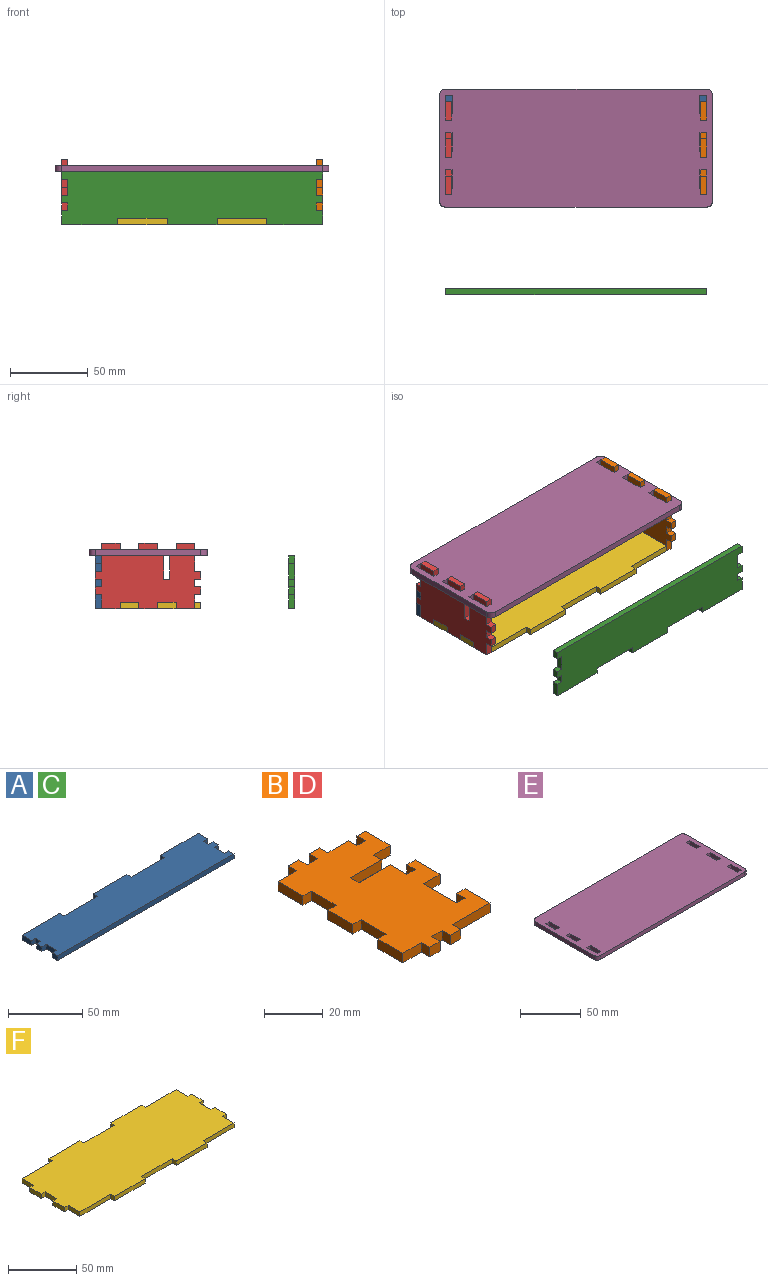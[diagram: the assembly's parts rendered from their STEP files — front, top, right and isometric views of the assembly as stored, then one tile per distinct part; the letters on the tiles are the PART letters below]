
ASSEMBLY  parts=6 mates=5
PART A: 30 faces, bbox 168x34x4 mm
  f0: plane 5x4mm, normal (1,0,0), area 20mm2, adj f1,f27,f28,f29
  f1: plane 4x4mm, normal (0,-1,0), area 16mm2, adj f0,f2,f28,f29
  f2: plane 9x4mm, normal (1,0,0), area 36mm2, adj f1,f3,f28,f29
  f3: plane 36x4mm, normal (0,1,0), area 144mm2, adj f2,f4,f28,f29
  f4: plane 4x4mm, normal (-1,0,0), area 16mm2, adj f3,f5,f28,f29
  f5: plane 32x4mm, normal (0,1,0), area 128mm2, adj f4,f6,f28,f29
  f6: plane 4x4mm, normal (1,0,0), area 16mm2, adj f5,f7,f28,f29
  f7: plane 32x4mm, normal (0,1,0), area 128mm2, adj f6,f8,f28,f29
  f8: plane 4x4mm, normal (-1,0,0), area 16mm2, adj f7,f9,f28,f29
  f9: plane 32x4mm, normal (0,1,0), area 128mm2, adj f8,f10,f28,f29
  f10: plane 4x4mm, normal (1,0,0), area 16mm2, adj f9,f11,f28,f29
  f11: plane 36x4mm, normal (0,1,0), area 144mm2, adj f10,f12,f28,f29
  f12: plane 9x4mm, normal (-1,0,0), area 36mm2, adj f11,f13,f28,f29
  f13: plane 4x4mm, normal (0,-1,0), area 16mm2, adj f12,f14,f28,f29
  f14: plane 5x4mm, normal (-1,0,0), area 20mm2, adj f13,f15,f28,f29
  f15: plane 4x4mm, normal (0,1,0), area 16mm2, adj f14,f16,f28,f29
  f16: plane 5x4mm, normal (-1,0,0), area 20mm2, adj f15,f17,f28,f29
  f17: plane 4x4mm, normal (0,-1,0), area 16mm2, adj f16,f18,f28,f29
  f18: plane 10x4mm, normal (-1,0,0), area 40mm2, adj f17,f19,f28,f29
  f19: plane 4x4mm, normal (0,1,0), area 16mm2, adj f18,f20,f28,f29
  f20: plane 5x4mm, normal (-1,0,0), area 20mm2, adj f19,f21,f28,f29
  f21: plane 168x4mm, normal (0,-1,0), area 672mm2, adj f20,f22,f28,f29
  f22: plane 5x4mm, normal (1,0,0), area 20mm2, adj f21,f23,f28,f29
  f23: plane 4x4mm, normal (0,1,0), area 16mm2, adj f22,f24,f28,f29
  f24: plane 10x4mm, normal (1,0,0), area 40mm2, adj f23,f25,f28,f29
  f25: plane 4x4mm, normal (0,-1,0), area 16mm2, adj f24,f26,f28,f29
  f26: plane 5x4mm, normal (1,0,0), area 20mm2, adj f25,f27,f28,f29
  f27: plane 4x4mm, normal (0,1,0), area 16mm2, adj f0,f26,f28,f29
  f28: plane 168x34mm, normal (0,0,1), area 5336mm2, adj f0,f1,f2,f3,f4,f5,f6,f7
  f29: plane 168x34mm, normal (0,0,-1), area 5336mm2, adj f0,f1,f2,f3,f4,f5,f6,f7
PART B: 50 faces, bbox 42x68x4 mm
  f0: plane 4x4mm, normal (1,0,0), area 16mm2, adj f1,f47,f48,f49
  f1: plane 8x4mm, normal (0,-1,0), area 32mm2, adj f0,f2,f48,f49
  f2: plane 12x4mm, normal (1,0,0), area 48mm2, adj f1,f3,f48,f49
  f3: plane 4x4mm, normal (0,1,0), area 16mm2, adj f2,f4,f48,f49
  f4: plane 4x4mm, normal (-1,0,0), area 16mm2, adj f3,f5,f48,f49
  f5: plane 4x4mm, normal (0,1,0), area 16mm2, adj f4,f6,f48,f49
  f6: plane 4x4mm, normal (1,0,0), area 16mm2, adj f5,f7,f48,f49
  f7: plane 10x4mm, normal (0,1,0), area 40mm2, adj f6,f8,f48,f49
  f8: plane 4x4mm, normal (1,0,0), area 16mm2, adj f7,f9,f48,f49
  f9: plane 5x4mm, normal (0,1,0), area 20mm2, adj f8,f10,f48,f49
  f10: plane 4x4mm, normal (-1,0,0), area 16mm2, adj f9,f11,f48,f49
  f11: plane 5x4mm, normal (0,1,0), area 20mm2, adj f10,f12,f48,f49
  f12: plane 4x4mm, normal (1,0,0), area 16mm2, adj f11,f13,f48,f49
  f13: plane 5x4mm, normal (0,1,0), area 20mm2, adj f12,f14,f48,f49
  f14: plane 4x4mm, normal (-1,0,0), area 16mm2, adj f13,f15,f48,f49
  f15: plane 9x4mm, normal (0,1,0), area 36mm2, adj f14,f16,f48,f49
  f16: plane 12x4mm, normal (-1,0,0), area 48mm2, adj f15,f17,f48,f49
  f17: plane 4x4mm, normal (0,-1,0), area 16mm2, adj f16,f18,f48,f49
  f18: plane 12x4mm, normal (-1,0,0), area 48mm2, adj f17,f19,f48,f49
  f19: plane 4x4mm, normal (0,1,0), area 16mm2, adj f18,f20,f48,f49
  f20: plane 12x4mm, normal (-1,0,0), area 48mm2, adj f19,f21,f48,f49
  f21: plane 4x4mm, normal (0,-1,0), area 16mm2, adj f20,f22,f48,f49
  f22: plane 12x4mm, normal (-1,0,0), area 48mm2, adj f21,f23,f48,f49
  f23: plane 4x4mm, normal (0,1,0), area 16mm2, adj f22,f24,f48,f49
  f24: plane 12x4mm, normal (-1,0,0), area 48mm2, adj f23,f25,f48,f49
  f25: plane 9x4mm, normal (0,-1,0), area 36mm2, adj f24,f26,f48,f49
  f26: plane 4x4mm, normal (-1,0,0), area 16mm2, adj f25,f27,f48,f49
  f27: plane 5x4mm, normal (0,-1,0), area 20mm2, adj f26,f28,f48,f49
  f28: plane 4x4mm, normal (1,0,0), area 16mm2, adj f27,f29,f48,f49
  f29: plane 5x4mm, normal (0,-1,0), area 20mm2, adj f28,f30,f48,f49
  f30: plane 4x4mm, normal (-1,0,0), area 16mm2, adj f29,f31,f48,f49
  f31: plane 5x4mm, normal (0,-1,0), area 20mm2, adj f30,f32,f48,f49
  f32: plane 4x4mm, normal (1,0,0), area 16mm2, adj f31,f33,f48,f49
  f33: plane 18x4mm, normal (0,-1,0), area 72mm2, adj f32,f34,f48,f49
  f34: plane 12x4mm, normal (1,0,0), area 48mm2, adj f33,f35,f48,f49
  f35: plane 4x4mm, normal (0,1,0), area 16mm2, adj f34,f36,f48,f49
  f36: plane 4x4mm, normal (-1,0,0), area 16mm2, adj f35,f37,f48,f49
  f37: plane 4x4mm, normal (0,1,0), area 16mm2, adj f36,f38,f48,f49
  f38: plane 16x4mm, normal (1,0,0), area 64mm2, adj f37,f39,f48,f49
  f39: plane 8x4mm, normal (0,-1,0), area 32mm2, adj f38,f40,f48,f49
  f40: plane 12x4mm, normal (1,0,0), area 48mm2, adj f39,f41,f48,f49
  f41: plane 4x4mm, normal (0,1,0), area 16mm2, adj f40,f42,f48,f49
  f42: plane 4x4mm, normal (-1,0,0), area 16mm2, adj f41,f43,f48,f49
  f43: plane 4x4mm, normal (0,1,0), area 16mm2, adj f42,f44,f48,f49
  f44: plane 8x4mm, normal (1,0,0), area 32mm2, adj f43,f45,f48,f49
  f45: plane 15x4mm, normal (0,1,0), area 60mm2, adj f44,f46,f48,f49
  f46: plane 4x4mm, normal (1,0,0), area 16mm2, adj f45,f47,f48,f49
  f47: plane 15x4mm, normal (0,-1,0), area 60mm2, adj f0,f46,f48,f49
  f48: plane 68x42mm, normal (0,0,1), area 2204mm2, adj f0,f1,f2,f3,f4,f5,f6,f7
  f49: plane 68x42mm, normal (0,0,-1), area 2204mm2, adj f0,f1,f2,f3,f4,f5,f6,f7
PART C: same geometry as A
PART D: same geometry as B
PART E: 34 faces, bbox 176x76x4 mm
  f0: plane 12x4mm, normal (-1,0,0), area 48mm2, adj f1,f27,f28,f29
  f1: plane 4.2x4mm, normal (0,1,0), area 16.8mm2, adj f0,f2,f28,f29
  f2: plane 12x4mm, normal (1,0,0), area 48mm2, adj f1,f27,f28,f29
  f3: plane 12x4mm, normal (-1,0,0), area 48mm2, adj f4,f21,f28,f29
  f4: plane 4.2x4mm, normal (0,1,0), area 16.8mm2, adj f3,f5,f28,f29
  f5: plane 12x4mm, normal (1,0,0), area 48mm2, adj f4,f21,f28,f29
  f6: plane 12x4mm, normal (1,0,0), area 48mm2, adj f7,f22,f28,f29
  f7: plane 4.2x4mm, normal (0,-1,0), area 16.8mm2, adj f6,f8,f28,f29
  f8: plane 12x4mm, normal (-1,0,0), area 48mm2, adj f7,f22,f28,f29
  f9: plane 68x4mm, normal (-1,0,0), area 272mm2, adj f28,f29,f30,f33
  f10: plane 168x4mm, normal (0,-1,0), area 672mm2, adj f28,f29,f30,f31
  f11: plane 68x4mm, normal (1,0,0), area 272mm2, adj f28,f29,f31,f32
  f12: plane 12x4mm, normal (-1,0,0), area 48mm2, adj f13,f24,f28,f29
  f13: plane 4.2x4mm, normal (0,1,0), area 16.8mm2, adj f12,f14,f28,f29
  f14: plane 12x4mm, normal (1,0,0), area 48mm2, adj f13,f24,f28,f29
  f15: plane 12x4mm, normal (-1,0,0), area 48mm2, adj f16,f25,f28,f29
  f16: plane 4.2x4mm, normal (0,1,0), area 16.8mm2, adj f15,f17,f28,f29
  f17: plane 12x4mm, normal (1,0,0), area 48mm2, adj f16,f25,f28,f29
  f18: plane 12x4mm, normal (-1,0,0), area 48mm2, adj f19,f26,f28,f29
  f19: plane 4.2x4mm, normal (0,1,0), area 16.8mm2, adj f18,f20,f28,f29
  f20: plane 12x4mm, normal (1,0,0), area 48mm2, adj f19,f26,f28,f29
  f21: plane 4.2x4mm, normal (0,-1,0), area 16.8mm2, adj f3,f5,f28,f29
  f22: plane 4.2x4mm, normal (0,1,0), area 16.8mm2, adj f6,f8,f28,f29
  f23: plane 168x4mm, normal (0,1,0), area 672mm2, adj f28,f29,f32,f33
  f24: plane 4.2x4mm, normal (0,-1,0), area 16.8mm2, adj f12,f14,f28,f29
  f25: plane 4.2x4mm, normal (0,-1,0), area 16.8mm2, adj f15,f17,f28,f29
  f26: plane 4.2x4mm, normal (0,-1,0), area 16.8mm2, adj f18,f20,f28,f29
  f27: plane 4.2x4mm, normal (0,-1,0), area 16.8mm2, adj f0,f2,f28,f29
  f28: plane 176x76mm, normal (0,0,1), area 13059.9mm2, adj f0,f1,f2,f3,f4,f5,f6,f7
  f29: plane 176x76mm, normal (0,0,-1), area 13059.9mm2, adj f0,f1,f2,f3,f4,f5,f6,f7
  f30: cylinder r=4mm len=4mm, axis (0,0,-1), area 25.1mm2, adj f9,f10,f28,f29
  f31: cylinder r=4mm len=4mm, axis (0,0,-1), area 25.1mm2, adj f10,f11,f28,f29
  f32: cylinder r=4mm len=4mm, axis (0,0,-1), area 25.1mm2, adj f11,f23,f28,f29
  f33: cylinder r=4mm len=4mm, axis (0,0,-1), area 25.1mm2, adj f9,f23,f28,f29
PART F: 38 faces, bbox 168x68x4 mm
  f0: plane 4x4mm, normal (-1,0,0), area 16mm2, adj f1,f35,f36,f37
  f1: plane 32x4mm, normal (0,-1,0), area 128mm2, adj f0,f2,f36,f37
  f2: plane 4x4mm, normal (1,0,0), area 16mm2, adj f1,f3,f36,f37
  f3: plane 32x4mm, normal (0,-1,0), area 128mm2, adj f2,f4,f36,f37
  f4: plane 4x4mm, normal (-1,0,0), area 16mm2, adj f3,f5,f36,f37
  f5: plane 32x4mm, normal (0,-1,0), area 128mm2, adj f4,f6,f36,f37
  f6: plane 4x4mm, normal (1,0,0), area 16mm2, adj f5,f7,f36,f37
  f7: plane 32x4mm, normal (0,-1,0), area 128mm2, adj f6,f8,f36,f37
  f8: plane 12x4mm, normal (1,0,0), area 48mm2, adj f7,f9,f36,f37
  f9: plane 4x4mm, normal (0,-1,0), area 16mm2, adj f8,f10,f36,f37
  f10: plane 12x4mm, normal (1,0,0), area 48mm2, adj f9,f11,f36,f37
  f11: plane 4x4mm, normal (0,1,0), area 16mm2, adj f10,f12,f36,f37
  f12: plane 12x4mm, normal (1,0,0), area 48mm2, adj f11,f13,f36,f37
  f13: plane 4x4mm, normal (0,-1,0), area 16mm2, adj f12,f14,f36,f37
  f14: plane 12x4mm, normal (1,0,0), area 48mm2, adj f13,f15,f36,f37
  f15: plane 4x4mm, normal (0,1,0), area 16mm2, adj f14,f16,f36,f37
  f16: plane 12x4mm, normal (1,0,0), area 48mm2, adj f15,f17,f36,f37
  f17: plane 32x4mm, normal (0,1,0), area 128mm2, adj f16,f18,f36,f37
  f18: plane 4x4mm, normal (1,0,0), area 16mm2, adj f17,f19,f36,f37
  f19: plane 32x4mm, normal (0,1,0), area 128mm2, adj f18,f20,f36,f37
  f20: plane 4x4mm, normal (-1,0,0), area 16mm2, adj f19,f21,f36,f37
  f21: plane 32x4mm, normal (0,1,0), area 128mm2, adj f20,f22,f36,f37
  f22: plane 4x4mm, normal (1,0,0), area 16mm2, adj f21,f23,f36,f37
  f23: plane 32x4mm, normal (0,1,0), area 128mm2, adj f22,f24,f36,f37
  f24: plane 4x4mm, normal (-1,0,0), area 16mm2, adj f23,f25,f36,f37
  f25: plane 32x4mm, normal (0,1,0), area 128mm2, adj f24,f26,f36,f37
  f26: plane 12x4mm, normal (-1,0,0), area 48mm2, adj f25,f27,f36,f37
  f27: plane 4x4mm, normal (0,1,0), area 16mm2, adj f26,f28,f36,f37
  f28: plane 12x4mm, normal (-1,0,0), area 48mm2, adj f27,f29,f36,f37
  f29: plane 4x4mm, normal (0,-1,0), area 16mm2, adj f28,f30,f36,f37
  f30: plane 12x4mm, normal (-1,0,0), area 48mm2, adj f29,f31,f36,f37
  f31: plane 4x4mm, normal (0,1,0), area 16mm2, adj f30,f32,f36,f37
  f32: plane 12x4mm, normal (-1,0,0), area 48mm2, adj f31,f33,f36,f37
  f33: plane 4x4mm, normal (0,-1,0), area 16mm2, adj f32,f34,f36,f37
  f34: plane 12x4mm, normal (-1,0,0), area 48mm2, adj f33,f35,f36,f37
  f35: plane 32x4mm, normal (0,-1,0), area 128mm2, adj f0,f34,f36,f37
  f36: plane 168x68mm, normal (0,0,1), area 10304mm2, adj f0,f1,f2,f3,f4,f5,f6,f7
  f37: plane 168x68mm, normal (0,0,-1), area 10304mm2, adj f0,f1,f2,f3,f4,f5,f6,f7
PLACE A rot(axis=(0,0.71,-0.71),180deg) t=(80,34,-30)mm
PLACE B rot(axis=(0.71,0,0.71),180deg) t=(80,30,-190)mm
PLACE C rot(axis=(-1,0,0),90deg) t=(-80,-94.5,-30)mm
PLACE D rot(axis=(0.71,0,0.71),180deg) t=(-84,30,-190)mm
PLACE E rot(axis=(1,0,0),180deg) t=(117.9,30,34)mm
PLACE F t=(-80,-30,-4)mm
MATE fastened F.f30 <-> D.f48  axis (-1,0,0) through (-80,0,-4)mm
MATE fastened B.f49 <-> F.f12  axis (-1,0,0) through (80,0,-4)mm
MATE fastened D.f43 <-> E.f7  axis (0,-1,0) through (-82,-2,32)mm
MATE fastened F.f21 <-> A.f28  axis (0,1,0) through (0,30,-4)mm
MATE slider F.f3 <-> C.f28  axis (0,-1,0) through (0,-30,-4)mm
